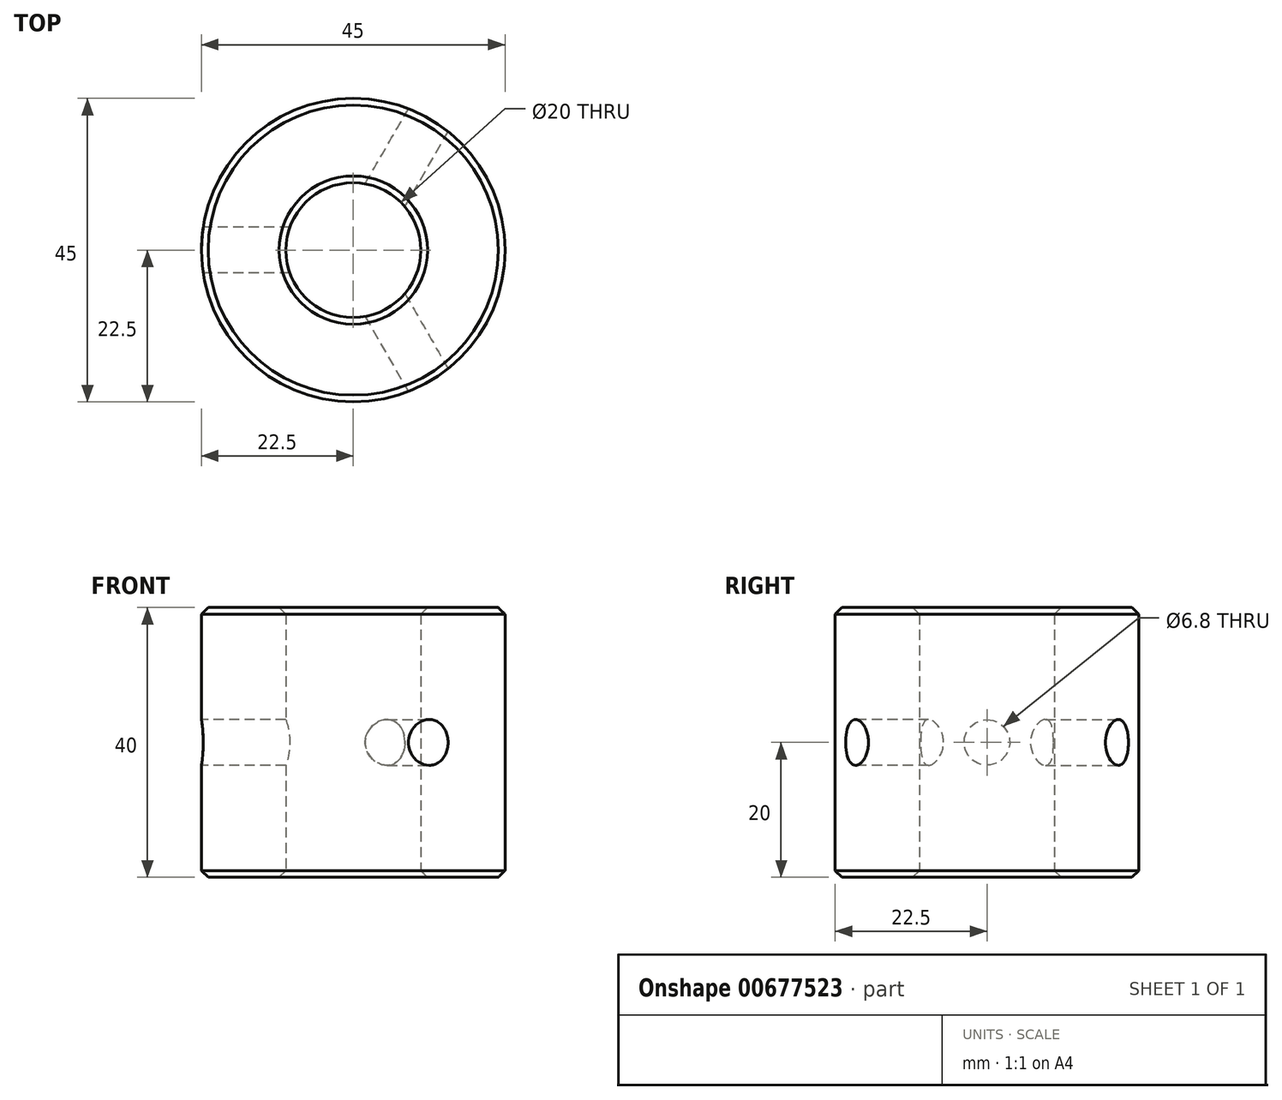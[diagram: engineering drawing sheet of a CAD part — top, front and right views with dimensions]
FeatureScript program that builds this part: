
annotation { "Feature Type Name" : "Feature", "Feature Type Description" : "" }
export const myFeature = defineFeature(function(context is Context, id is Id, definition is map)
    precondition{}
    {
        {
            var Q0;
            Q0=qCreatedBy(makeId("Top.planeOp"),FACE);
            var sketch = newSketch(context, id + "F0", { "sketchPlane" : qUnion([Q0])});
            skCircle(sketch, "E0", {"center": v(0, 0) * mm, "radius": 22.5 * mm});
            skCircle(sketch, "E1", {"center": v(0, 0) * mm, "radius": 10 * mm});
            skLineSegment(sketch, "E2", {"start": v(0, 0) * mm, "end": v(56.05, 0) * mm, "construction": true});
            skLineSegment(sketch, "E3", {"start": v(0, 0) * mm, "end": v(-25.82, 44.73) * mm, "construction": true});
            skLineSegment(sketch, "E4", {"start": v(-20.85, -36.1) * mm, "end": v(0, 0) * mm, "construction": true});
            skPoint(sketch, "E5", {"position": v(11.25, 19.49) * mm});
            skPoint(sketch, "E6", {"position": v(-22.5, 0) * mm});
            skPoint(sketch, "E7", {"position": v(11.25, -19.49) * mm});
            skLineSegment(sketch, "E8", {"start": v(0, 0) * mm, "end": v(22.76, 39.42) * mm, "construction": true});
            skLineSegment(sketch, "E9", {"start": v(0, 0) * mm, "end": v(-38.24, 0) * mm, "construction": true});
            skLineSegment(sketch, "E10", {"start": v(0, 0) * mm, "end": v(20.42, -35.36) * mm, "construction": true});
            skSolve(sketch);
        }
        {
            var Q0;
            Q0=makeQuery(id+"F0.imprint","IMPRINT",FACE,{"disambiguationData":[TD([[makeQuery(id+"F0.imprint","IMPRINT",EDGE,{"derivedFrom":sQuery(id+"F0.wireOp",EDGE,"E0")}),1.0]])]});
            extrude(context, id + "F1", {"entities" : qUnion([Q0]), "depth" : 40 * mm, "offsetDistance" : 25 * mm, "symmetric" : true});
        }
        {
            var Q0;
            Q0=makeQuery(id+"F1.opExtrude","CAP_EDGE",EDGE,{"disambiguationData":[OSD([sQuery(id+"F0.wireOp",EDGE,"E0")])],"isStart":false});
            var Q1;
            Q1=makeQuery(id+"F1.opExtrude","CAP_EDGE",EDGE,{"disambiguationData":[OSD([sQuery(id+"F0.wireOp",EDGE,"E0")])],"isStart":true});
            var Q2;
            Q2=makeQuery(id+"F1.opExtrude","CAP_EDGE",EDGE,{"disambiguationData":[OSD([sQuery(id+"F0.wireOp",EDGE,"E1")])],"isStart":false});
            var Q3;
            Q3=makeQuery(id+"F1.opExtrude","CAP_EDGE",EDGE,{"disambiguationData":[OSD([sQuery(id+"F0.wireOp",EDGE,"E1")])],"isStart":true});
            chamfer(context, id + "F2", {"entities" : qUnion([Q0, Q1, Q2, Q3]), "width" : 1 * mm, "tangentPropagation" : true});
        }
        {
            var Q0;
            Q0=sQuery(id+"F0.wireOp",VERTEX,"E7");
            var Q1;
            Q1=sQuery(id+"F0.wireOp",EDGE,"E10");
            cPlane(context, id + "F3", {"entities" : qUnion([Q0, Q1]), "cplaneType" : CPlaneType.LINE_POINT, "offset" : 25 * mm, "width" : 150 * mm, "height" : 150 * mm});
        }
        {
            var Q0;
            Q0=qCreatedBy(id+"F3.planeOp",FACE);
            var sketch = newSketch(context, id + "F4", { "sketchPlane" : qUnion([Q0])});
            skPoint(sketch, "E11", {"position": v(0, 0) * mm});
            skSolve(sketch);
        }
        {
            var Q0;
            Q0=sQuery(id+"F0.wireOp",EDGE,"E8");
            cPoint(context, id + "F5", {"entities" : qUnion([Q0]), "parameter" : 0.5});
        }
        {
            var Q0;
            Q0 = qCreatedBy(id + "F5" ,VERTEX);
            var Q1;
            Q1=sQuery(id+"F0.wireOp",EDGE,"E8");
            cPlane(context, id + "F6", {"entities" : qUnion([Q0, Q1]), "cplaneType" : CPlaneType.LINE_POINT, "offset" : 25 * mm, "width" : 150 * mm, "height" : 150 * mm});
        }
        {
            var Q0;
            Q0=qCreatedBy(id+"F6.planeOp",FACE);
            var sketch = newSketch(context, id + "F7", { "sketchPlane" : qUnion([Q0])});
            skPoint(sketch, "E12", {"position": v(0, 0) * mm});
            skSolve(sketch);
        }
        {
            var Q0;
            Q0=sQuery(id+"F0.wireOp",VERTEX,"E6");
            var Q1;
            Q1=sQuery(id+"F0.wireOp",EDGE,"E9");
            cPlane(context, id + "F8", {"entities" : qUnion([Q0, Q1]), "cplaneType" : CPlaneType.LINE_POINT, "offset" : 25 * mm, "width" : 150 * mm, "height" : 150 * mm});
        }
        {
            var Q0;
            Q0=qCreatedBy(id+"F8.planeOp",FACE);
            var sketch = newSketch(context, id + "F9", { "sketchPlane" : qUnion([Q0])});
            skPoint(sketch, "E13", {"position": v(0, 0) * mm});
            skSolve(sketch);
        }
        {
            var Q0;
            Q0=sQuery(id+"F4.wireOp",VERTEX,"E11");
            var Q1;
            Q1=sQuery(id+"F7.wireOp",VERTEX,"E12");
            var Q2;
            Q2=sQuery(id+"F9.wireOp",VERTEX,"E13");
            var Q3;
            Q3=makeQuery(id+"F1.opExtrude","SWEPT_BODY",BODY,{"disambiguationData":[OSD([sQuery(id+"F0.wireOp",EDGE,"E0"),sQuery(id+"F0.wireOp",EDGE,"E1")])]});
            hole(context, id + "F10", {"style" : HoleStyle.SIMPLE, "endStyle" : HoleEndStyle.BLIND, "standardTappedOrClearance" : lookupTablePath({ "standard" : "ISO", "engagement" : "75%", "pitch" : "1.25 mm", "size" : "M8", "type" : "Tapped" }), "standardBlindInLast" : lookupTablePath({ "standard" : "ISO", "engagement" : "75%", "pitch" : "1.25 mm", "size" : "M8", "type" : "Tapped" }), "holeDiameter" : 6.8 * mm, "majorDiameter" : 8 * mm, "showTappedDepth" : true, "holeDepth" : 15 * mm, "isTappedThrough" : true, "tappedDepth" : 11.25 * mm, "tapClearance" : 3, "startFromSketch" : true, "locations" : qUnion([Q0, Q1, Q2]), "scope" : qUnion([Q3])});
        }
    });
